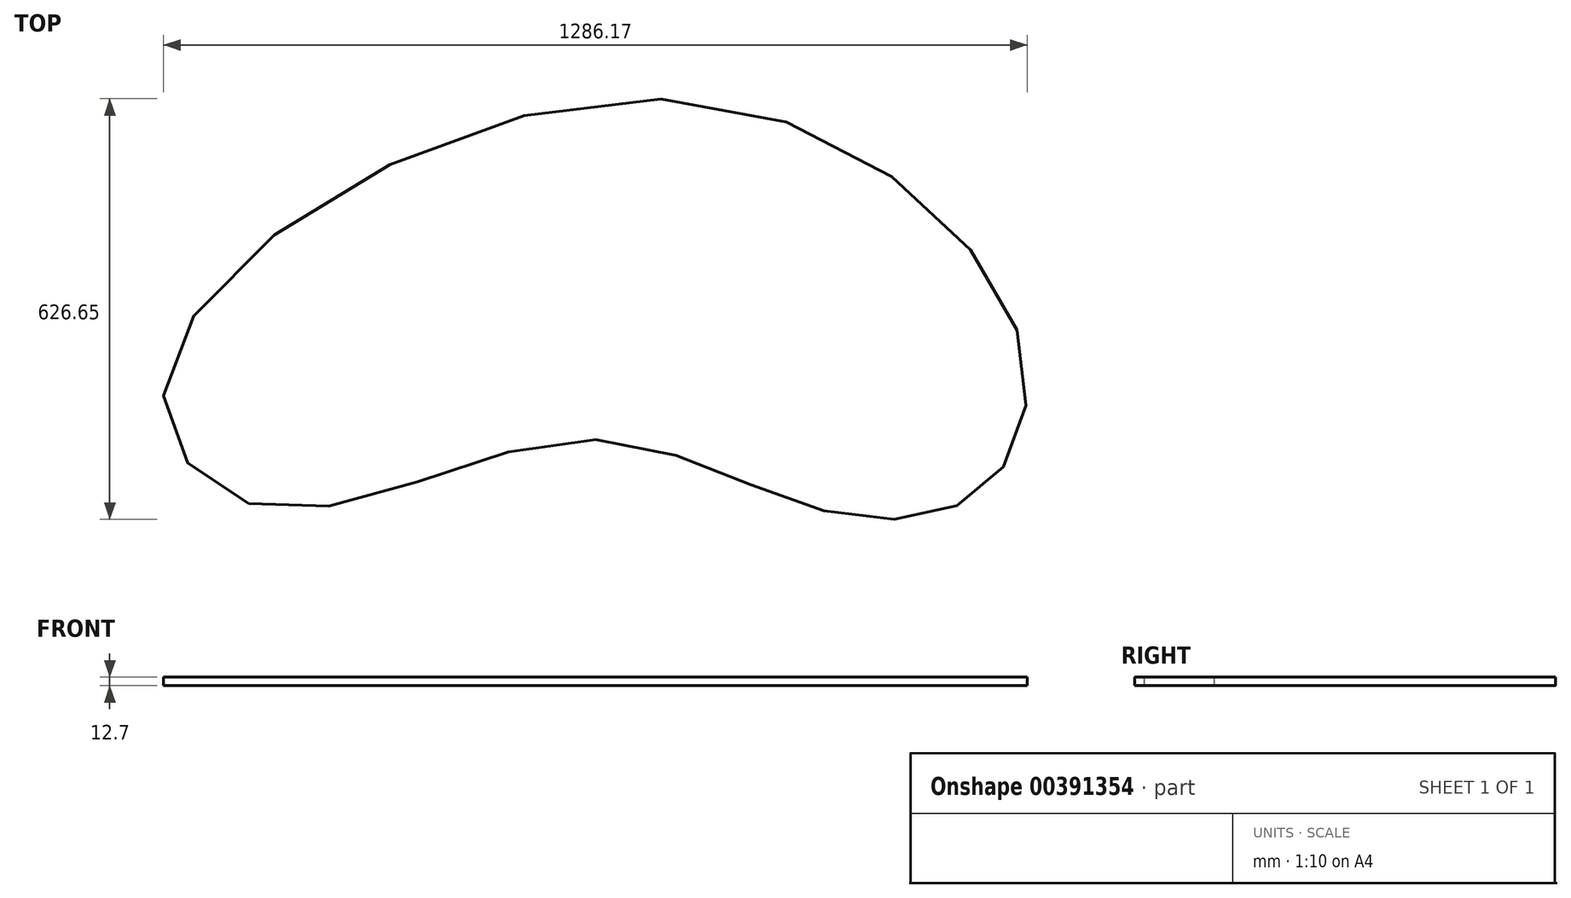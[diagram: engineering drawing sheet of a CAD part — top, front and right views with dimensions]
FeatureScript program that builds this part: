
annotation { "Feature Type Name" : "Feature", "Feature Type Description" : "" }
export const myFeature = defineFeature(function(context is Context, id is Id, definition is map)
    precondition{}
    {
        {
            var Q0;
            Q0=qCreatedBy(makeId("Top.planeOp"),FACE);
            var sketch = newSketch(context, id + "F0", { "sketchPlane" : qUnion([Q0])});
            skLineSegment(sketch, "E0.bottom", {"start": v(0, 0) * mm, "end": v(1270, 0) * mm, "construction": true});
            skLineSegment(sketch, "E0.top", {"start": v(0, 609.6) * mm, "end": v(1270, 609.6) * mm, "construction": true});
            skLineSegment(sketch, "E0.left", {"start": v(0, 0) * mm, "end": v(0, 609.6) * mm, "construction": true});
            skLineSegment(sketch, "E0.right", {"start": v(1270, 0) * mm, "end": v(1270, 609.6) * mm, "construction": true});
            skLineSegment(sketch, "E1", {"start": v(1270, 254) * mm, "end": v(0, 254) * mm, "construction": true});
            skLineSegment(sketch, "E2", {"start": v(965.2, 609.6) * mm, "end": v(965.2, 0) * mm, "construction": true});
            skLineSegment(sketch, "E3", {"start": v(736.6, 609.6) * mm, "end": v(736.6, 0) * mm, "construction": true});
            skLineSegment(sketch, "E4", {"start": v(152.4, 609.6) * mm, "end": v(152.4, 0) * mm, "construction": true});
            skLineSegment(sketch, "E5", {"start": v(1270, 101.6) * mm, "end": v(0, 101.6) * mm, "construction": true});
            skLineSegment(sketch, "E6", {"start": v(609.6, 609.6) * mm, "end": v(609.6, 0) * mm, "construction": true});
            skLineSegment(sketch, "E7", {"start": v(1270, 203.2) * mm, "end": v(0, 203.2) * mm, "construction": true});
            skFitSpline(sketch, "E8", {"points": [v(736.6, 609.6) * mm, v(0, 203.2) * mm, v(152.4, 0) * mm, v(609.6, 101.6) * mm, v(965.2, 0) * mm, v(1208.1, 22.03) * mm, v(1270, 254) * mm, v(736.6, 609.6) * mm]});
            skSolve(sketch);
        }
        {
            var Q0;
            Q0=makeQuery(id+"F0.imprint","IMPRINT",FACE,{"disambiguationData":[TD([[makeQuery(id+"F0.imprint","IMPRINT",EDGE,{"derivedFrom":sQuery(id+"F0.wireOp",EDGE,"E8")}),1.0]])]});
            extrude(context, id + "F1", {"entities" : qUnion([Q0]), "oppositeDirection" : true, "depth" : 12.7 * mm});
        }
    });
